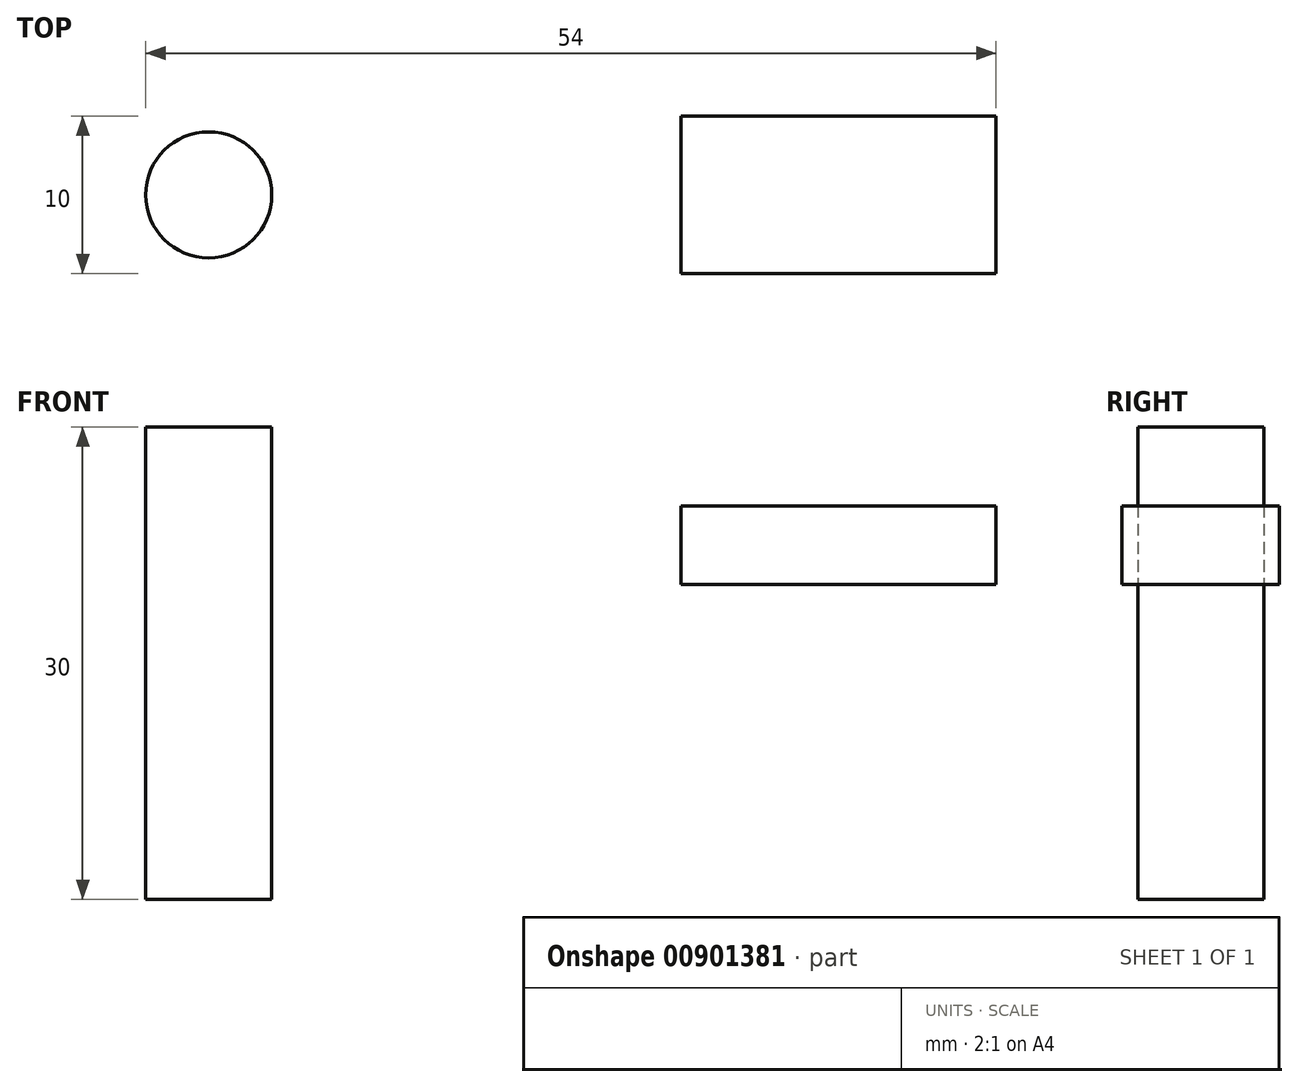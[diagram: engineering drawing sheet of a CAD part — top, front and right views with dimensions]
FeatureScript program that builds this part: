
annotation { "Feature Type Name" : "Feature", "Feature Type Description" : "" }
export const myFeature = defineFeature(function(context is Context, id is Id, definition is map)
    precondition{}
    {
        {
            var Q0;
            Q0=qCreatedBy(makeId("Top.planeOp"),FACE);
            var sketch = newSketch(context, id + "F0", { "sketchPlane" : qUnion([Q0])});
            skLineSegment(sketch, "E0.bottom", {"start": v(30, 5) * mm, "end": v(50, 5) * mm});
            skLineSegment(sketch, "E0.top", {"start": v(30, -5) * mm, "end": v(50, -5) * mm});
            skLineSegment(sketch, "E0.left", {"start": v(30, 5) * mm, "end": v(30, -5) * mm});
            skLineSegment(sketch, "E0.right", {"start": v(50, 5) * mm, "end": v(50, -5) * mm});
            skCircle(sketch, "E1", {"center": v(0, 0) * mm, "radius": 4 * mm});
            skSolve(sketch);
        }
        {
            var Q0;
            Q0=makeQuery(id+"F0.imprint","IMPRINT",FACE,{"disambiguationData":[TD([[makeQuery(id+"F0.imprint","IMPRINT",EDGE,{"derivedFrom":sQuery(id+"F0.wireOp",EDGE,"E0.bottom")}),-1.0]])]});
            var Q1;
            Q1 = qSketchRegion(id + "F2", true);
            extrude(context, id + "F1", {"entities" : qUnion([Q0, Q1]), "depth" : 5 * mm, "offsetDistance" : 25 * mm});
        }
        {
            var Q0;
            Q0=qCreatedBy(makeId("Right.planeOp"),FACE);
            var sketch = newSketch(context, id + "F2", { "sketchPlane" : qUnion([Q0])});
            skLineSegment(sketch, "E2", {"start": v(0, 20.86) * mm, "end": v(0, -19.63) * mm});
            skSolve(sketch);
        }
        {
            var Q0;
            Q0=makeQuery(id+"F0.imprint","IMPRINT",FACE,{"disambiguationData":[TD([[makeQuery(id+"F0.imprint","IMPRINT",EDGE,{"derivedFrom":sQuery(id+"F0.wireOp",EDGE,"E1")}),1.0]])]});
            extrude(context, id + "F3", {"entities" : qUnion([Q0]), "depth" : 10 * mm, "offsetDistance" : 25 * mm, "hasSecondDirection" : true, "secondDirectionOppositeDirection" : true, "secondDirectionDepth" : 20 * mm});
        }
    });
